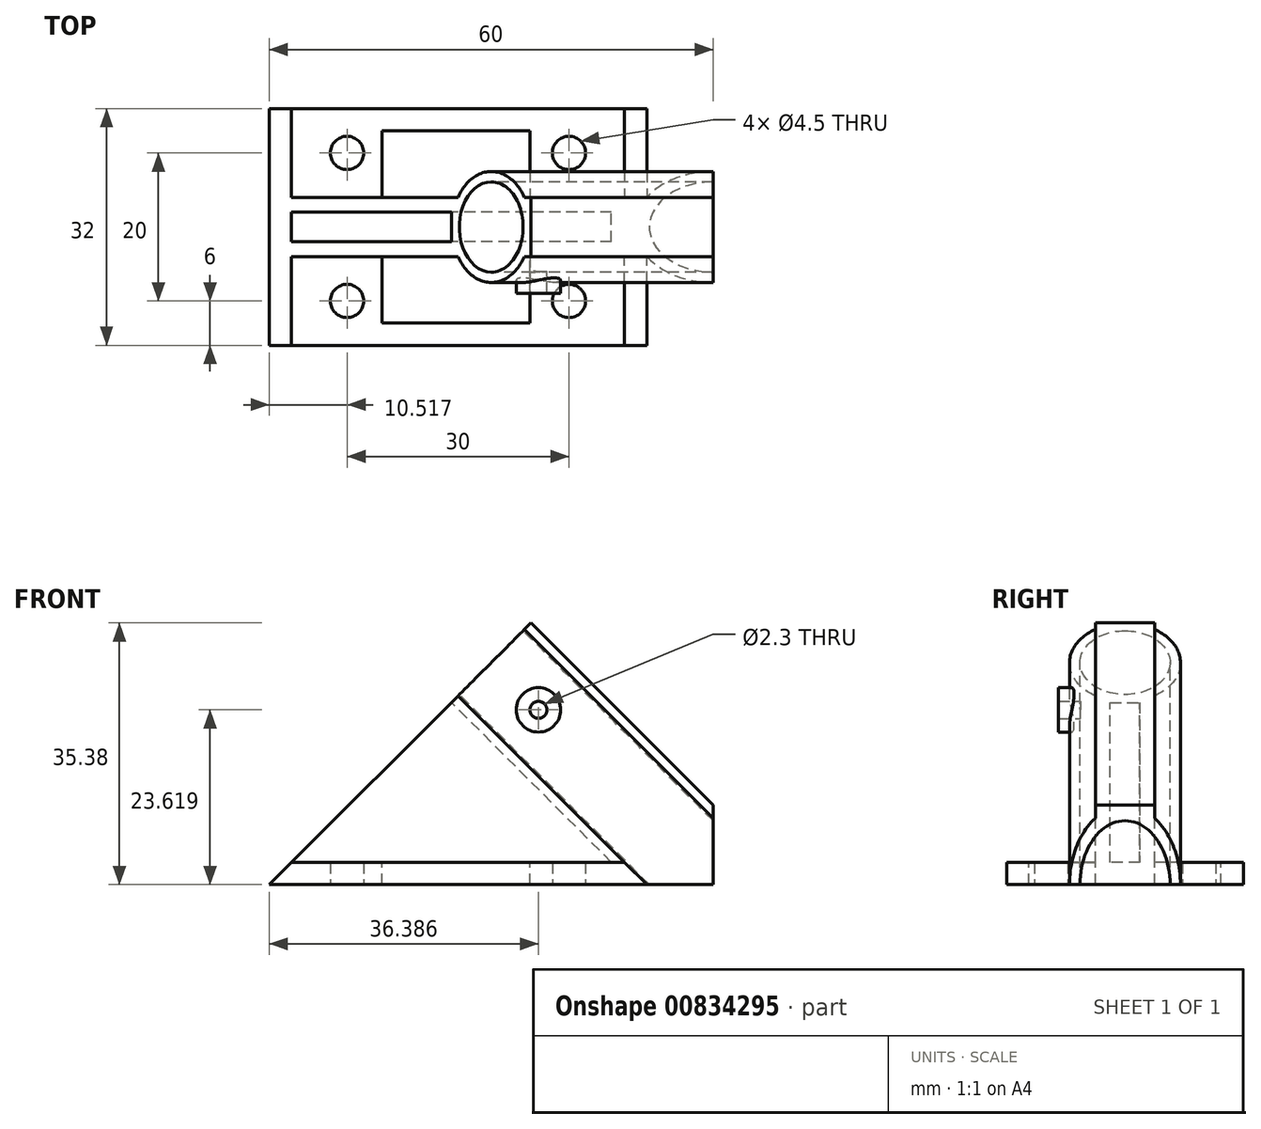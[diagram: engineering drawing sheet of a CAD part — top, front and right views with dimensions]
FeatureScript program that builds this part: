
annotation { "Feature Type Name" : "Feature", "Feature Type Description" : "" }
export const myFeature = defineFeature(function(context is Context, id is Id, definition is map)
    precondition{}
    {
        {
            var Q0;
            Q0=qCreatedBy(makeId("Front.planeOp"),FACE);
            var sketch = newSketch(context, id + "F0", { "sketchPlane" : qUnion([Q0])});
            skLineSegment(sketch, "E0", {"start": v(0, 0) * mm, "end": v(60, 0) * mm});
            skLineSegment(sketch, "E1", {"start": v(60, 0) * mm, "end": v(60, 60) * mm});
            skLineSegment(sketch, "E2", {"start": v(60, 60) * mm, "end": v(0, 0) * mm});
            skSolve(sketch);
        }
        {
            var Q0;
            Q0=makeQuery(id+"F0.imprint","IMPRINT",FACE,{"disambiguationData":[TD([[makeQuery(id+"F0.imprint","IMPRINT",EDGE,{"derivedFrom":sQuery(id+"F0.wireOp",EDGE,"E0")}),1.0]])]});
            extrude(context, id + "F1", {"entities" : qUnion([Q0]), "depth" : 60 * mm, "offsetDistance" : 25 * mm});
        }
        {
            var Q0;
            Q0=makeQuery(id+"F1.opExtrude","SWEPT_FACE",FACE,{"disambiguationData":[OSD([sQuery(id+"F0.wireOp",EDGE,"E2")])]});
            var sketch = newSketch(context, id + "F2", { "sketchPlane" : qUnion([Q0])});
            skLineSegment(sketch, "E3", {"start": v(0, 0) * mm, "end": v(26, 0) * mm});
            skLineSegment(sketch, "E4", {"start": v(26, 0) * mm, "end": v(26, 36.09) * mm});
            skArc(sketch, "E5", {"start": v(26, 48.77) * mm, "mid": v(22.5, 42.43) * mm, "end": v(26, 36.09) * mm});
            skLineSegment(sketch, "E6", {"start": v(26, 36.09) * mm, "end": v(26, 48.77) * mm, "construction": true});
            skLineSegment(sketch, "E7", {"start": v(26, 48.77) * mm, "end": v(26, 84.85) * mm});
            skLineSegment(sketch, "E8", {"start": v(26, 84.85) * mm, "end": v(0, 84.85) * mm});
            skLineSegment(sketch, "E9", {"start": v(0, 84.85) * mm, "end": v(0, 0) * mm});
            skLineSegment(sketch, "E10", {"start": v(34, 48.77) * mm, "end": v(34, 84.85) * mm});
            skLineSegment(sketch, "E11", {"start": v(34, 84.85) * mm, "end": v(60, 84.85) * mm});
            skLineSegment(sketch, "E12", {"start": v(60, 84.85) * mm, "end": v(60, 0) * mm});
            skLineSegment(sketch, "E13", {"start": v(60, 0) * mm, "end": v(34, 0) * mm});
            skLineSegment(sketch, "E14", {"start": v(34, 0) * mm, "end": v(34, 36.09) * mm});
            skArc(sketch, "E15", {"start": v(34, 36.09) * mm, "mid": v(37.5, 42.43) * mm, "end": v(34, 48.77) * mm});
            skLineSegment(sketch, "E16", {"start": v(34, 36.09) * mm, "end": v(34, 48.77) * mm, "construction": true});
            skLineSegment(sketch, "E17", {"start": v(30, 42.43) * mm, "end": v(60, 42.43) * mm, "construction": true});
            skLineSegment(sketch, "E18", {"start": v(30, 42.43) * mm, "end": v(0, 42.43) * mm, "construction": true});
            skSolve(sketch);
        }
        {
            var Q0;
            Q0 = qSketchRegion(id + "F2", true);
            extrude(context, id + "F3", {"entities" : qUnion([Q0]), "operationType" : NewBodyOperationType.REMOVE, "endBound" : BoundingType.UP_TO_NEXT, "oppositeDirection" : true, "depth" : 25 * mm, "offsetDistance" : 25 * mm});
        }
        {
            var Q0;
            Q0=makeQuery(id+"F3.boolean.opBoolean","COPY",FACE,{"derivedFrom":makeQuery(id+"F3.opExtrude","SWEPT_FACE",FACE,{"disambiguationData":[OSD([sQuery(id+"F2.wireOp",EDGE,"E14")])]})});
            var sketch = newSketch(context, id + "F4", { "sketchPlane" : qUnion([Q0])});
            skCircle(sketch, "E19", {"center": v(36.39, 23.62) * mm, "radius": 3 * mm});
            skLineSegment(sketch, "E20", {"start": v(36.39, 23.62) * mm, "end": v(40.87, 28.1) * mm, "construction": true});
            skLineSegment(sketch, "E21", {"start": v(36.39, 23.62) * mm, "end": v(31.9, 19.13) * mm, "construction": true});
            skSolve(sketch);
        }
        {
            var Q0;
            Q0 = qSketchRegion(id + "F4", true);
            extrude(context, id + "F5", {"entities" : qUnion([Q0]), "operationType" : NewBodyOperationType.ADD, "depth" : 5 * mm, "offsetDistance" : 25 * mm});
        }
        {
            var Q0;
            Q0=makeQuery(id+"F1.opExtrude","SWEPT_FACE",FACE,{"disambiguationData":[OSD([sQuery(id+"F0.wireOp",EDGE,"E2")])]});
            var sketch = newSketch(context, id + "F6", { "sketchPlane" : qUnion([Q0])});
            skCircle(sketch, "E22", {"center": v(30, 42.43) * mm, "radius": 6.1 * mm});
            skSolve(sketch);
        }
        {
            var Q0;
            Q0 = qSketchRegion(id + "F6", true);
            extrude(context, id + "F7", {"entities" : qUnion([Q0]), "operationType" : NewBodyOperationType.REMOVE, "endBound" : BoundingType.UP_TO_NEXT, "oppositeDirection" : true, "depth" : 25 * mm, "offsetDistance" : 25 * mm});
        }
        {
            var Q0;
            {var subQ0=sQuery(id+"F10.wireOp",EDGE,"E30");Q0=makeQuery(id+"F12.boolean.opBoolean","MERGE",FACE,{"derivedFrom":[makeQuery(id+"F11.boolean.opBoolean","MERGE",FACE,{"derivedFrom":[makeQuery(id+"F1.opExtrude","SWEPT_FACE",FACE,{"disambiguationData":[OSD([sQuery(id+"F0.wireOp",EDGE,"E2")])]}),makeQuery(id+"F11.opExtrude","SWEPT_FACE",FACE,{"disambiguationData":[OSD([subQ0])]})]}),makeQuery(id+"F12.opExtrude","SWEPT_FACE",FACE,{"disambiguationData":[OSD([subQ0])]})]});}
            var sketch = newSketch(context, id + "F8", { "sketchPlane" : qUnion([Q0])});
            skLineSegment(sketch, "E23", {"start": v(28, 34.83) * mm, "end": v(28, 4.24) * mm});
            skLineSegment(sketch, "E24", {"start": v(28, 4.24) * mm, "end": v(32, 4.24) * mm});
            skLineSegment(sketch, "E25", {"start": v(32, 4.24) * mm, "end": v(32, 34.83) * mm});
            skLineSegment(sketch, "E26", {"start": v(32, 34.83) * mm, "end": v(28, 34.83) * mm});
            skLineSegment(sketch, "E27", {"start": v(26, 4.24) * mm, "end": v(28, 4.24) * mm, "construction": true});
            skLineSegment(sketch, "E28", {"start": v(34, 4.24) * mm, "end": v(32, 4.24) * mm, "construction": true});
            skLineSegment(sketch, "E29.bottom", {"start": v(26, 84.85) * mm, "end": v(34, 84.85) * mm});
            skLineSegment(sketch, "E29.top", {"start": v(26, 50.03) * mm, "end": v(34, 50.03) * mm});
            skLineSegment(sketch, "E29.left", {"start": v(26, 84.85) * mm, "end": v(26, 50.03) * mm});
            skLineSegment(sketch, "E29.right", {"start": v(34, 84.85) * mm, "end": v(34, 50.03) * mm});
            skSolve(sketch);
        }
        {
            var Q0;
            Q0 = qSketchRegion(id + "F8", true);
            extrude(context, id + "F9", {"entities" : qUnion([Q0]), "operationType" : NewBodyOperationType.REMOVE, "endBound" : BoundingType.UP_TO_NEXT, "oppositeDirection" : true, "depth" : 25 * mm, "offsetDistance" : 25 * mm});
        }
        {
            var Q0;
            Q0=makeQuery(id+"F3.boolean.opBoolean","COPY",FACE,{"derivedFrom":makeQuery(id+"F3.opExtrude","SWEPT_FACE",FACE,{"disambiguationData":[OSD([sQuery(id+"F2.wireOp",EDGE,"E14")])]})});
            var sketch = newSketch(context, id + "F10", { "sketchPlane" : qUnion([Q0])});
            skLineSegment(sketch, "E30", {"start": v(0, 0) * mm, "end": v(3, 3) * mm});
            skLineSegment(sketch, "E31", {"start": v(3, 3) * mm, "end": v(48.03, 3) * mm});
            skLineSegment(sketch, "E32", {"start": v(48.03, 3) * mm, "end": v(51.03, 0) * mm});
            skLineSegment(sketch, "E33", {"start": v(51.03, 0) * mm, "end": v(0, 0) * mm});
            skSolve(sketch);
        }
        {
            var Q0;
            Q0 = qSketchRegion(id + "F10", true);
            extrude(context, id + "F11", {"entities" : qUnion([Q0]), "operationType" : NewBodyOperationType.ADD, "depth" : 12 * mm, "offsetDistance" : 25 * mm});
        }
        {
            var Q0;
            Q0 = qSketchRegion(id + "F10", true);
            extrude(context, id + "F12", {"entities" : qUnion([Q0]), "operationType" : NewBodyOperationType.ADD, "oppositeDirection" : true, "depth" : 20 * mm, "offsetDistance" : 25 * mm});
        }
        {
            var Q0;
            {var subQ0=sQuery(id+"F10.wireOp",EDGE,"E33");Q0=makeQuery(id+"F12.boolean.opBoolean","MERGE",FACE,{"derivedFrom":[makeQuery(id+"F11.boolean.opBoolean","MERGE",FACE,{"derivedFrom":[makeQuery(id+"F1.opExtrude","SWEPT_FACE",FACE,{"disambiguationData":[OSD([sQuery(id+"F0.wireOp",EDGE,"E0")])]}),makeQuery(id+"F11.opExtrude","SWEPT_FACE",FACE,{"disambiguationData":[OSD([subQ0])]})]}),makeQuery(id+"F12.opExtrude","SWEPT_FACE",FACE,{"disambiguationData":[OSD([subQ0])]})]});}
            var sketch = newSketch(context, id + "F13", { "sketchPlane" : qUnion([Q0])});
            skCircle(sketch, "E34", {"center": v(10.52, 40) * mm, "radius": 2.25 * mm});
            skCircle(sketch, "E35", {"center": v(40.52, 40) * mm, "radius": 2.25 * mm});
            skCircle(sketch, "E36", {"center": v(40.52, 20) * mm, "radius": 2.25 * mm});
            skCircle(sketch, "E37", {"center": v(10.52, 20) * mm, "radius": 2.25 * mm});
            skLineSegment(sketch, "E38", {"start": v(10.52, 40) * mm, "end": v(40.52, 40) * mm, "construction": true});
            skLineSegment(sketch, "E39", {"start": v(40.52, 40) * mm, "end": v(40.52, 20) * mm, "construction": true});
            skLineSegment(sketch, "E40", {"start": v(10.52, 20) * mm, "end": v(40.52, 20) * mm, "construction": true});
            skLineSegment(sketch, "E41", {"start": v(10.52, 40) * mm, "end": v(10.52, 20) * mm, "construction": true});
            skLineSegment(sketch, "E42", {"start": v(40.52, 40) * mm, "end": v(51.03, 40) * mm, "construction": true});
            skLineSegment(sketch, "E43", {"start": v(10.52, 40) * mm, "end": v(10.52, 46) * mm, "construction": true});
            skLineSegment(sketch, "E44", {"start": v(10.52, 20) * mm, "end": v(0, 20) * mm, "construction": true});
            skLineSegment(sketch, "E45", {"start": v(40.52, 20) * mm, "end": v(40.52, 14) * mm, "construction": true});
            skSolve(sketch);
        }
        {
            var Q0;
            Q0 = qSketchRegion(id + "F13", true);
            extrude(context, id + "F14", {"entities" : qUnion([Q0]), "operationType" : NewBodyOperationType.REMOVE, "endBound" : BoundingType.UP_TO_NEXT, "oppositeDirection" : true, "depth" : 25 * mm, "offsetDistance" : 25 * mm});
        }
        {
            var Q0;
            Q0=makeQuery(id+"F11.opExtrude","SWEPT_FACE",FACE,{"disambiguationData":[OSD([sQuery(id+"F10.wireOp",EDGE,"E31")])]});
            var sketch = newSketch(context, id + "F15", { "sketchPlane" : qUnion([Q0])});
            skLineSegment(sketch, "E46.bottom", {"start": v(35.27, -17) * mm, "end": v(15.27, -17) * mm});
            skLineSegment(sketch, "E46.top", {"start": v(35.27, -26) * mm, "end": v(15.27, -26) * mm});
            skLineSegment(sketch, "E46.left", {"start": v(35.27, -17) * mm, "end": v(35.27, -26) * mm});
            skLineSegment(sketch, "E46.right", {"start": v(15.27, -17) * mm, "end": v(15.27, -26) * mm});
            skLineSegment(sketch, "E47.bottom", {"start": v(35.27, -34) * mm, "end": v(15.27, -34) * mm});
            skLineSegment(sketch, "E47.top", {"start": v(35.27, -43) * mm, "end": v(15.27, -43) * mm});
            skLineSegment(sketch, "E47.left", {"start": v(35.27, -34) * mm, "end": v(35.27, -43) * mm});
            skLineSegment(sketch, "E47.right", {"start": v(15.27, -34) * mm, "end": v(15.27, -43) * mm});
            skSolve(sketch);
        }
        {
            var Q0;
            Q0 = qSketchRegion(id + "F15", true);
            extrude(context, id + "F16", {"entities" : qUnion([Q0]), "operationType" : NewBodyOperationType.REMOVE, "endBound" : BoundingType.UP_TO_NEXT, "oppositeDirection" : true, "depth" : 25 * mm, "offsetDistance" : 25 * mm});
        }
        {
            var Q0;
            Q0=makeQuery(id+"F16.boolean.opBoolean","MERGE",FACE,{"derivedFrom":[makeQuery(id+"F3.boolean.opBoolean","COPY",FACE,{"derivedFrom":makeQuery(id+"F3.opExtrude","SWEPT_FACE",FACE,{"disambiguationData":[OSD([sQuery(id+"F2.wireOp",EDGE,"E14")])]})})],"fromTools":[makeQuery(id+"F16.opExtrude","SWEPT_FACE",FACE,{"disambiguationData":[OSD([sQuery(id+"F15.wireOp",EDGE,"E47.bottom")])]})]});
            var sketch = newSketch(context, id + "F17", { "sketchPlane" : qUnion([Q0])});
            skCircle(sketch, "E48", {"center": v(36.39, 23.62) * mm, "radius": 1.15 * mm});
            skLineSegment(sketch, "E49", {"start": v(36.39, 23.62) * mm, "end": v(40.87, 28.1) * mm, "construction": true});
            skLineSegment(sketch, "E50", {"start": v(36.39, 23.62) * mm, "end": v(31.9, 19.13) * mm, "construction": true});
            skLineSegment(sketch, "E51", {"start": v(36.39, 23.62) * mm, "end": v(36.39, 3) * mm, "construction": true});
            skSolve(sketch);
        }
        {
            var Q0;
            Q0 = qSketchRegion(id + "F17", true);
            extrude(context, id + "F18", {"entities" : qUnion([Q0]), "operationType" : NewBodyOperationType.REMOVE, "depth" : 25 * mm, "offsetDistance" : 25 * mm});
        }
    });
